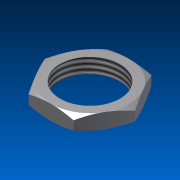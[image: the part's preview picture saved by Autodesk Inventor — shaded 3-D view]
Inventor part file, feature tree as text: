
AUTODESK INVENTOR PART (.ipt)
format: ipt  version: 2011 SP1 (Build 150282100, 282)  size: 134,656 bytes
history: native  units: mm
features: sketch x2, extrude x1, thread x1, revolve x1
ambient origin geometry x8: Origin, YZ Plane, XZ Plane, XY Plane, X Axis, Y Axis, Z Axis, Center Point
bodies: Solid1 (feature_tree)
feature tree (5):
  extrude  "Extrusion1"  TaperAngle=120.0deg  [1 undecoded]
  thread  "Thread1"  [1 undecoded]
  revolve  "Revolution1"  [1 undecoded]
  sketch  "Sketch1"  dims[d0=6.0mm d1=120.0deg d2=120.0deg]
  sketch  "Sketch2"  dims[d5=4.5mm d6=4.5mm d7=4.5mm d8=1.5mm d9=0.0mm d10=10.0mm d11=0.0mm d12=0.3mm d13=0.3mm d14=0.6mm d15=0.6mm d16=90.0deg d17=4.5mm d18=4.5mm d19=4.5mm d20=7.794229mm d21=3.897114mm]
note: 3 required parameter values undecoded (feature->parameter linkage not recoverable at this tier; creation-order binding heuristic only, values carry confidence <= 0.55)